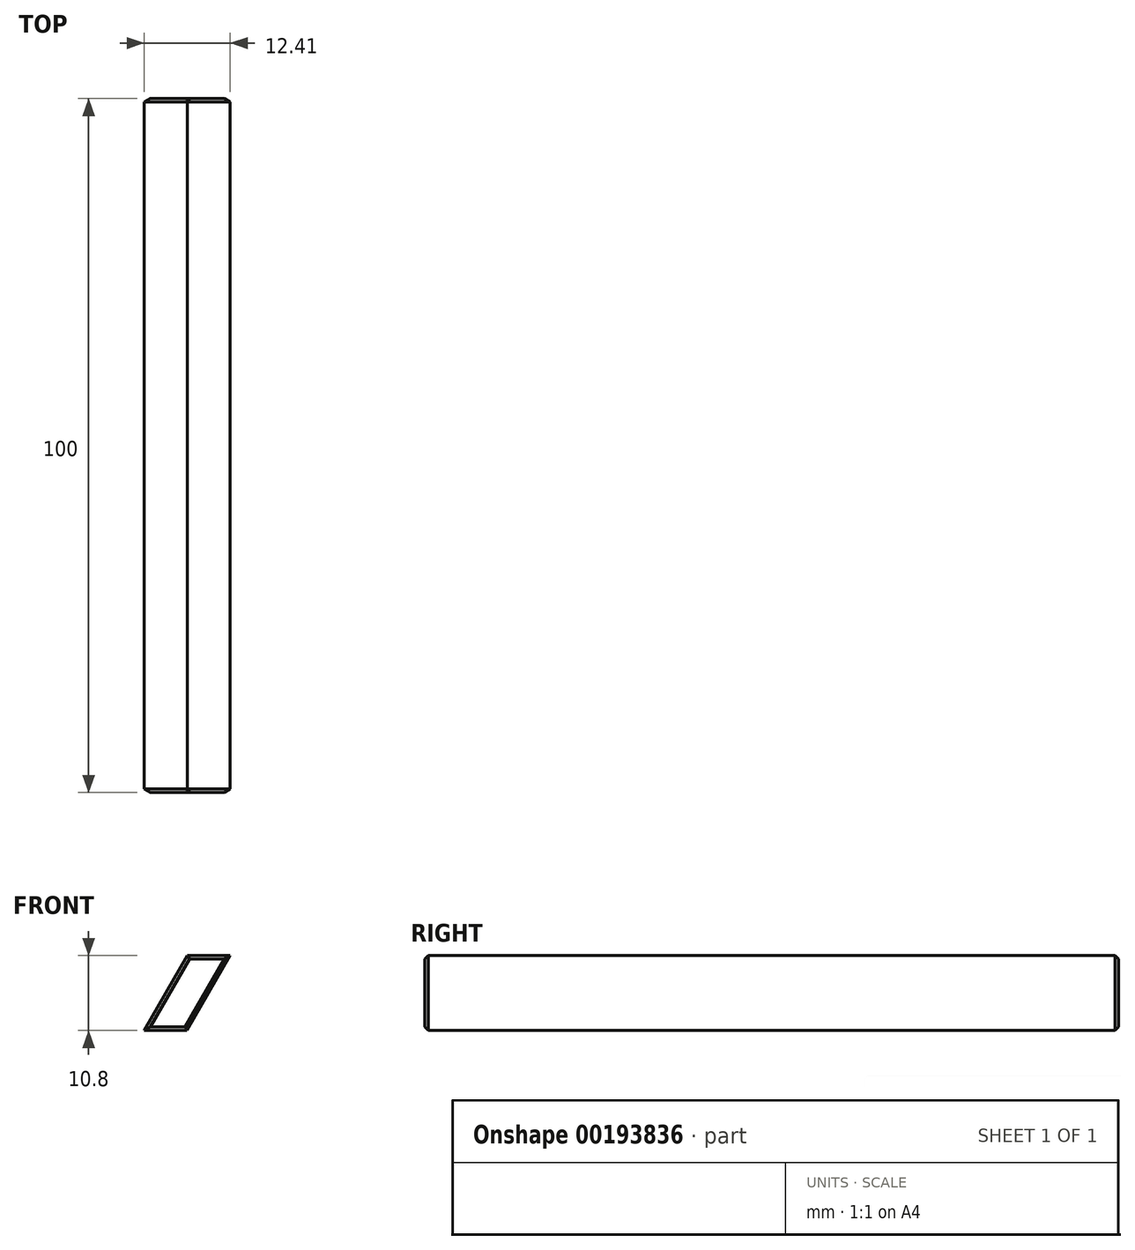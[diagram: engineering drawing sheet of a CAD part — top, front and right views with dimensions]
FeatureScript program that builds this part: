
annotation { "Feature Type Name" : "Feature", "Feature Type Description" : "" }
export const myFeature = defineFeature(function(context is Context, id is Id, definition is map)
    precondition{}
    {
        {
            var Q0;
            Q0=qCreatedBy(makeId("Front.planeOp"),FACE);
            var sketch = newSketch(context, id + "F0", { "sketchPlane" : qUnion([Q0])});
            skLineSegment(sketch, "E0", {"start": v(0, 0) * mm, "end": v(6.18, 0) * mm});
            skLineSegment(sketch, "E1", {"start": v(0, 0) * mm, "end": v(6.24, 10.8) * mm});
            skLineSegment(sketch, "E2", {"start": v(6.18, 0) * mm, "end": v(12.41, 10.8) * mm});
            skLineSegment(sketch, "E3", {"start": v(6.24, 10.8) * mm, "end": v(12.41, 10.8) * mm});
            skLineSegment(sketch, "E4", {"start": v(0, 0) * mm, "end": v(9.1, -5.25) * mm, "construction": true});
            skLineSegment(sketch, "E5", {"start": v(12.41, 10.8) * mm, "end": v(17.39, 7.93) * mm, "construction": true});
            skSolve(sketch);
        }
        {
            var Q0;
            Q0=makeQuery(id+"F0.imprint","IMPRINT",FACE,{"disambiguationData":[TD([[makeQuery(id+"F0.imprint","IMPRINT",EDGE,{"derivedFrom":sQuery(id+"F0.wireOp",EDGE,"E0")}),1.0]])]});
            extrude(context, id + "F1", {"entities" : qUnion([Q0]), "depth" : 100 * mm});
        }
        {
            var Q0;
            Q0=makeQuery(id+"F1.opExtrude","CAP_EDGE",EDGE,{"disambiguationData":[OSD([sQuery(id+"F0.wireOp",EDGE,"E3")])],"isStart":false});
            var Q1;
            Q1=makeQuery(id+"F1.opExtrude","CAP_EDGE",EDGE,{"disambiguationData":[OSD([sQuery(id+"F0.wireOp",EDGE,"E1")])],"isStart":false});
            var Q2;
            Q2=makeQuery(id+"F1.opExtrude","CAP_EDGE",EDGE,{"disambiguationData":[OSD([sQuery(id+"F0.wireOp",EDGE,"E2")])],"isStart":false});
            var Q3;
            Q3=makeQuery(id+"F1.opExtrude","CAP_EDGE",EDGE,{"disambiguationData":[OSD([sQuery(id+"F0.wireOp",EDGE,"E0")])],"isStart":false});
            var Q4;
            Q4=makeQuery(id+"F1.opExtrude","CAP_EDGE",EDGE,{"disambiguationData":[OSD([sQuery(id+"F0.wireOp",EDGE,"E2")])],"isStart":true});
            var Q5;
            Q5=makeQuery(id+"F1.opExtrude","CAP_EDGE",EDGE,{"disambiguationData":[OSD([sQuery(id+"F0.wireOp",EDGE,"E1")])],"isStart":true});
            var Q6;
            Q6=makeQuery(id+"F1.opExtrude","CAP_EDGE",EDGE,{"disambiguationData":[OSD([sQuery(id+"F0.wireOp",EDGE,"E0")])],"isStart":true});
            var Q7;
            Q7=makeQuery(id+"F1.opExtrude","CAP_EDGE",EDGE,{"disambiguationData":[OSD([sQuery(id+"F0.wireOp",EDGE,"E3")])],"isStart":true});
            chamfer(context, id + "F2", {"entities" : qUnion([Q0, Q1, Q2, Q3, Q4, Q5, Q6, Q7]), "width" : .5 * mm, "tangentPropagation" : true});
        }
    });
